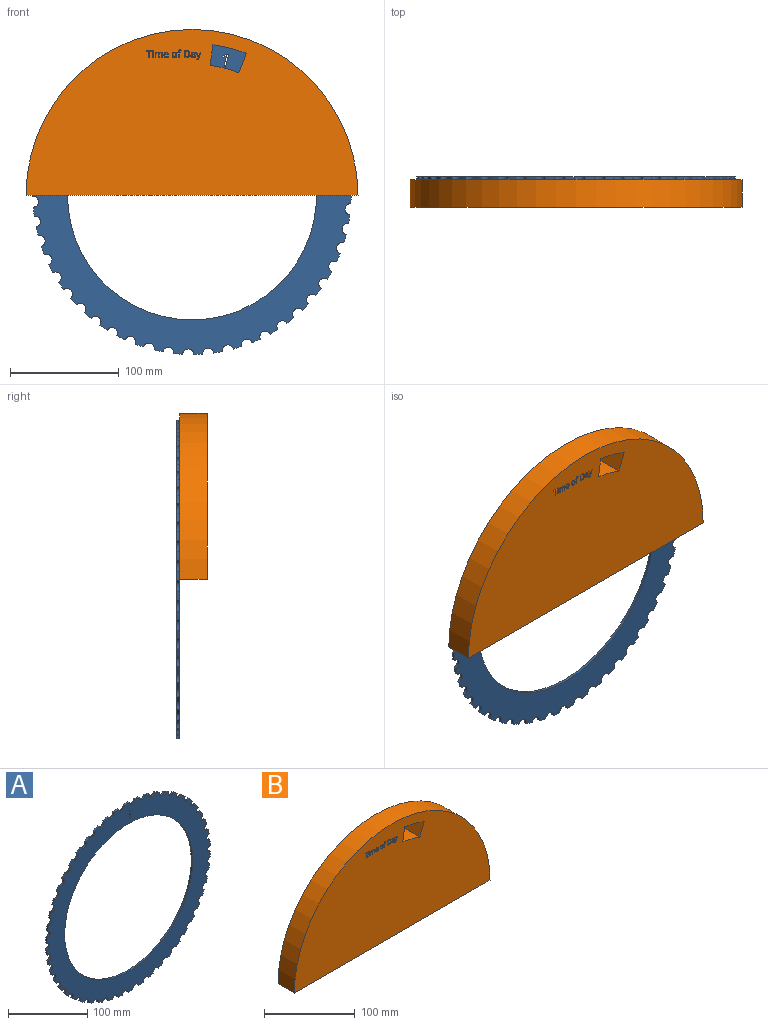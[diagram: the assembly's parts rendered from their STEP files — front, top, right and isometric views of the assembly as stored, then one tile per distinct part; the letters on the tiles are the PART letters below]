
ASSEMBLY  parts=2 mates=1
PART A: 112 faces, bbox 292.1x2.5x292.1 mm
  f0: plane 292.1x292.08mm, normal (0,-1,0), area 23935.8mm2, adj f2,f3,f4,f5,f6,f7,f8,f9
  f1: plane 292.1x292.08mm, normal (0,1,0), area 23935.8mm2, adj f2,f3,f4,f5,f6,f7,f8,f9
  f2: cylinder r=146.05mm len=7.98mm, axis (0,1,0), area 20.8mm2, adj f0,f1,f5,f101
  f3: cylinder r=146.05mm len=7.68mm, axis (0,1,0), area 20.8mm2, adj f0,f1,f4,f5
  f4: cylinder r=5.08mm len=9.69mm, axis (0,-1,0), area 40.1mm2, adj f0,f1,f3,f6
  f5: cylinder r=5.08mm len=9.92mm, axis (0,-1,0), area 40.1mm2, adj f0,f1,f2,f3
  f6: cylinder r=146.05mm len=7.27mm, axis (0,1,0), area 20.8mm2, adj f0,f1,f4,f9
  f7: cylinder r=146.05mm len=6.73mm, axis (0,1,0), area 20.8mm2, adj f0,f1,f8,f9
  f8: cylinder r=5.08mm len=9.01mm, axis (0,-1,0), area 40.1mm2, adj f0,f1,f7,f10
  f9: cylinder r=5.08mm len=9.38mm, axis (0,-1,0), area 40.1mm2, adj f0,f1,f6,f7
  f10: cylinder r=146.05mm len=6.1mm, axis (0,1,0), area 20.8mm2, adj f0,f1,f8,f13
  f11: cylinder r=146.05mm len=6.19mm, axis (0,1,0), area 20.8mm2, adj f0,f1,f12,f13
  f12: cylinder r=5.08mm len=9.07mm, axis (0,-1,0), area 40.1mm2, adj f0,f1,f11,f14
  f13: cylinder r=5.08mm len=8.64mm, axis (0,-1,0), area 40.1mm2, adj f0,f1,f10,f11
  f14: cylinder r=146.05mm len=6.82mm, axis (0,1,0), area 20.8mm2, adj f0,f1,f12,f17
  f15: cylinder r=146.05mm len=7.33mm, axis (0,1,0), area 20.8mm2, adj f0,f1,f16,f17
  f16: cylinder r=5.08mm len=9.73mm, axis (0,-1,0), area 40.1mm2, adj f0,f1,f15,f18
  f17: cylinder r=5.08mm len=9.43mm, axis (0,-1,0), area 40.1mm2, adj f0,f1,f14,f15
  f18: cylinder r=146.05mm len=7.73mm, axis (0,1,0), area 20.8mm2, adj f0,f1,f16,f21
  f19: cylinder r=146.05mm len=8.01mm, axis (0,1,0), area 20.8mm2, adj f0,f1,f20,f21
  f20: cylinder r=5.08mm len=10.09mm, axis (0,-1,0), area 40.1mm2, adj f0,f1,f19,f22
  f21: cylinder r=5.08mm len=9.95mm, axis (0,-1,0), area 40.1mm2, adj f0,f1,f18,f19
  f22: cylinder r=146.05mm len=8.16mm, axis (0,1,0), area 20.8mm2, adj f0,f1,f20,f25
  f23: cylinder r=146.05mm len=8.19mm, axis (0,1,0), area 20.8mm2, adj f0,f1,f24,f25
  f24: cylinder r=5.08mm len=10.12mm, axis (0,-1,0), area 40.1mm2, adj f0,f1,f23,f26
  f25: cylinder r=5.08mm len=10.16mm, axis (0,-1,0), area 40.1mm2, adj f0,f1,f22,f23
  f26: cylinder r=146.05mm len=8.08mm, axis (0,1,0), area 20.8mm2, adj f0,f1,f24,f29
  f27: cylinder r=146.05mm len=7.85mm, axis (0,1,0), area 20.8mm2, adj f0,f1,f28,f29
  f28: cylinder r=5.08mm len=9.81mm, axis (0,-1,0), area 40.1mm2, adj f0,f1,f27,f30
  f29: cylinder r=5.08mm len=10.01mm, axis (0,-1,0), area 40.1mm2, adj f0,f1,f26,f27
  f30: cylinder r=146.05mm len=7.49mm, axis (0,1,0), area 20.8mm2, adj f0,f1,f28,f33
  f31: cylinder r=146.05mm len=7.01mm, axis (0,1,0), area 20.8mm2, adj f0,f1,f32,f33
  f32: cylinder r=5.08mm len=9.21mm, axis (0,-1,0), area 40.1mm2, adj f0,f1,f31,f34
  f33: cylinder r=5.08mm len=9.54mm, axis (0,-1,0), area 40.1mm2, adj f0,f1,f30,f31
  f34: cylinder r=146.05mm len=6.43mm, axis (0,1,0), area 20.8mm2, adj f0,f1,f32,f37
  f35: cylinder r=146.05mm len=5.84mm, axis (0,1,0), area 20.8mm2, adj f0,f1,f36,f37
  f36: cylinder r=5.08mm len=8.86mm, axis (0,-1,0), area 40.1mm2, adj f0,f1,f35,f38
  f37: cylinder r=5.08mm len=8.8mm, axis (0,-1,0), area 40.1mm2, adj f0,f1,f34,f35
  f38: cylinder r=146.05mm len=6.52mm, axis (0,1,0), area 20.8mm2, adj f0,f1,f36,f41
  f39: cylinder r=146.05mm len=7.09mm, axis (0,1,0), area 20.8mm2, adj f0,f1,f40,f41
  f40: cylinder r=5.08mm len=9.59mm, axis (0,-1,0), area 40.1mm2, adj f0,f1,f39,f42
  f41: cylinder r=5.08mm len=9.26mm, axis (0,-1,0), area 40.1mm2, adj f0,f1,f38,f39
  f42: cylinder r=146.05mm len=7.55mm, axis (0,1,0), area 20.8mm2, adj f0,f1,f40,f45
  f43: cylinder r=146.05mm len=7.89mm, axis (0,1,0), area 20.8mm2, adj f0,f1,f44,f45
  f44: cylinder r=5.08mm len=10.03mm, axis (0,-1,0), area 40.1mm2, adj f0,f1,f43,f46
  f45: cylinder r=5.08mm len=9.85mm, axis (0,-1,0), area 40.1mm2, adj f0,f1,f42,f43
  f46: cylinder r=146.05mm len=8.1mm, axis (0,1,0), area 20.8mm2, adj f0,f1,f44,f49
  f47: cylinder r=146.05mm len=8.19mm, axis (0,1,0), area 20.8mm2, adj f0,f1,f48,f49
  f48: cylinder r=5.08mm len=10.15mm, axis (0,-1,0), area 40.1mm2, adj f0,f1,f47,f50
  f49: cylinder r=5.08mm len=10.13mm, axis (0,-1,0), area 40.1mm2, adj f0,f1,f46,f47
  f50: cylinder r=146.05mm len=8.15mm, axis (0,1,0), area 20.8mm2, adj f0,f1,f48,f53
  f51: cylinder r=146.05mm len=7.98mm, axis (0,1,0), area 20.8mm2, adj f0,f1,f52,f53
  f52: cylinder r=5.08mm len=9.92mm, axis (0,-1,0), area 40.1mm2, adj f0,f1,f51,f54
  f53: cylinder r=5.08mm len=10.07mm, axis (0,-1,0), area 40.1mm2, adj f0,f1,f50,f51
  f54: cylinder r=146.05mm len=7.68mm, axis (0,1,0), area 20.8mm2, adj f0,f1,f52,f57
  f55: cylinder r=146.05mm len=7.27mm, axis (0,1,0), area 20.8mm2, adj f0,f1,f56,f57
  f56: cylinder r=5.08mm len=9.38mm, axis (0,-1,0), area 40.1mm2, adj f0,f1,f55,f58
  f57: cylinder r=5.08mm len=9.69mm, axis (0,-1,0), area 40.1mm2, adj f0,f1,f54,f55
  f58: cylinder r=146.05mm len=6.73mm, axis (0,1,0), area 20.8mm2, adj f0,f1,f56,f61
  f59: cylinder r=146.05mm len=6.1mm, axis (0,1,0), area 20.8mm2, adj f0,f1,f60,f61
  f60: cylinder r=5.08mm len=8.64mm, axis (0,-1,0), area 40.1mm2, adj f0,f1,f59,f62
  f61: cylinder r=5.08mm len=9.01mm, axis (0,-1,0), area 40.1mm2, adj f0,f1,f58,f59
  f62: cylinder r=146.05mm len=6.19mm, axis (0,1,0), area 20.8mm2, adj f0,f1,f60,f65
  f63: cylinder r=146.05mm len=6.82mm, axis (0,1,0), area 20.8mm2, adj f0,f1,f64,f65
  f64: cylinder r=5.08mm len=9.43mm, axis (0,-1,0), area 40.1mm2, adj f0,f1,f63,f66
  f65: cylinder r=5.08mm len=9.07mm, axis (0,-1,0), area 40.1mm2, adj f0,f1,f62,f63
  f66: cylinder r=146.05mm len=7.33mm, axis (0,1,0), area 20.8mm2, adj f0,f1,f64,f69
  f67: cylinder r=146.05mm len=7.73mm, axis (0,1,0), area 20.8mm2, adj f0,f1,f68,f69
  f68: cylinder r=5.08mm len=9.95mm, axis (0,-1,0), area 40.1mm2, adj f0,f1,f67,f70
  f69: cylinder r=5.08mm len=9.73mm, axis (0,-1,0), area 40.1mm2, adj f0,f1,f66,f67
  f70: cylinder r=146.05mm len=8.01mm, axis (0,1,0), area 20.8mm2, adj f0,f1,f68,f73
  f71: cylinder r=146.05mm len=8.16mm, axis (0,1,0), area 20.8mm2, adj f0,f1,f72,f73
  f72: cylinder r=5.08mm len=10.16mm, axis (0,-1,0), area 40.1mm2, adj f0,f1,f71,f74
  f73: cylinder r=5.08mm len=10.09mm, axis (0,-1,0), area 40.1mm2, adj f0,f1,f70,f71
  f74: cylinder r=146.05mm len=8.19mm, axis (0,1,0), area 20.8mm2, adj f0,f1,f72,f77
  f75: cylinder r=146.05mm len=8.08mm, axis (0,1,0), area 20.8mm2, adj f0,f1,f76,f77
  f76: cylinder r=5.08mm len=10.01mm, axis (0,-1,0), area 40.1mm2, adj f0,f1,f75,f78
  f77: cylinder r=5.08mm len=10.12mm, axis (0,-1,0), area 40.1mm2, adj f0,f1,f74,f75
  f78: cylinder r=146.05mm len=7.85mm, axis (0,1,0), area 20.8mm2, adj f0,f1,f76,f81
  f79: cylinder r=146.05mm len=7.49mm, axis (0,1,0), area 20.8mm2, adj f0,f1,f80,f81
  f80: cylinder r=5.08mm len=9.54mm, axis (0,-1,0), area 40.1mm2, adj f0,f1,f79,f82
  f81: cylinder r=5.08mm len=9.81mm, axis (0,-1,0), area 40.1mm2, adj f0,f1,f78,f79
  f82: cylinder r=146.05mm len=7.01mm, axis (0,1,0), area 20.8mm2, adj f0,f1,f80,f85
  f83: cylinder r=146.05mm len=6.43mm, axis (0,1,0), area 20.8mm2, adj f0,f1,f84,f85
  f84: cylinder r=5.08mm len=8.8mm, axis (0,-1,0), area 40.1mm2, adj f0,f1,f83,f86
  f85: cylinder r=5.08mm len=9.21mm, axis (0,-1,0), area 40.1mm2, adj f0,f1,f82,f83
  f86: cylinder r=146.05mm len=5.84mm, axis (0,1,0), area 20.8mm2, adj f0,f1,f84,f89
  f87: cylinder r=146.05mm len=6.52mm, axis (0,1,0), area 20.8mm2, adj f0,f1,f88,f89
  f88: cylinder r=5.08mm len=9.26mm, axis (0,-1,0), area 40.1mm2, adj f0,f1,f87,f90
  f89: cylinder r=5.08mm len=8.86mm, axis (0,-1,0), area 40.1mm2, adj f0,f1,f86,f87
  f90: cylinder r=146.05mm len=7.09mm, axis (0,1,0), area 20.8mm2, adj f0,f1,f88,f93
  f91: cylinder r=146.05mm len=7.55mm, axis (0,1,0), area 20.8mm2, adj f0,f1,f92,f93
  f92: cylinder r=5.08mm len=9.85mm, axis (0,-1,0), area 40.1mm2, adj f0,f1,f91,f94
  f93: cylinder r=5.08mm len=9.59mm, axis (0,-1,0), area 40.1mm2, adj f0,f1,f90,f91
  f94: cylinder r=146.05mm len=7.89mm, axis (0,1,0), area 20.8mm2, adj f0,f1,f92,f97
  f95: cylinder r=146.05mm len=8.1mm, axis (0,1,0), area 20.8mm2, adj f0,f1,f96,f97
  f96: cylinder r=5.08mm len=10.13mm, axis (0,-1,0), area 40.1mm2, adj f0,f1,f95,f98
  f97: cylinder r=5.08mm len=10.03mm, axis (0,-1,0), area 40.1mm2, adj f0,f1,f94,f95
  f98: cylinder r=146.05mm len=8.19mm, axis (0,1,0), area 20.8mm2, adj f0,f1,f96,f102
  f99: cylinder r=114.3mm len=228.6mm, axis (0,1,0), area 1824.1mm2, adj f0,f1
  f100: cylinder r=146.05mm len=8.15mm, axis (0,1,0), area 20.8mm2, adj f0,f1,f101,f102
  f101: cylinder r=5.08mm len=10.07mm, axis (0,-1,0), area 40.1mm2, adj f0,f1,f2,f100
  f102: cylinder r=5.08mm len=10.15mm, axis (0,-1,0), area 40.1mm2, adj f0,f1,f98,f100
  f103: plane 2.54x1.37mm, normal (0,0,1), area 3.5mm2, adj f0,f1,f104,f111
  f104: plane 12.41x2.54mm, normal (-1,0,0), area 31.5mm2, adj f0,f1,f103,f105
  f105: plane 2.54x1.19mm, normal (0,0,-1), area 3mm2, adj f0,f1,f104,f106
  f106: plane 3.28x2.54mm, normal (0.61,0,-0.79), area 10.5mm2, adj f0,f1,f105,f107
  f107: plane 2.54x0.97mm, normal (0.79,0,0.61), area 3.1mm2, adj f0,f1,f106,f108
  f108: extruded ~2.54x2.02mm, area 6.6mm2, adj f0,f1,f107,f109
  f109: extruded ~2.54x0.4mm, area 1.4mm2, adj f0,f1,f108,f110
  f110: extruded ~2.54x2.09mm, area 5.3mm2, adj f0,f1,f109,f111
  f111: plane 8.84x2.54mm, normal (1,0,0), area 22.5mm2, adj f0,f1,f103,f110
PART B: 180 faces, bbox 304.8x25.4x152.4 mm
  f0: plane 304.8x152.4mm, normal (0,-1,0), area 35806.5mm2, adj f1,f2,f4,f5,f6,f7,f8,f9
  f1: cylinder r=152.4mm len=304.8mm, axis (0,1,0), area 12161mm2, adj f0,f2,f3
  f2: plane 304.8x25.4mm, normal (0,0,-1), area 7741.9mm2, adj f0,f1,f3
  f3: plane 304.8x152.4mm, normal (0,1,0), area 35920.5mm2, adj f1,f2,f176,f177,f178,f179
  f4: plane 5.08x0.79mm, normal (0,0,-1), area 4mm2, adj f0,f5,f19,f20
  f5: plane 5.08x4.87mm, normal (0.93,0,0.37), area 26.7mm2, adj f0,f4,f6,f20
  f6: plane 5.08x0.69mm, normal (0.93,0,-0.37), area 3.8mm2, adj f0,f5,f7,f20
  f7: extruded ~5.08x1.08mm, area 7.5mm2, adj f0,f6,f8,f20
  f8: extruded ~5.08x0.54mm, area 2.8mm2, adj f0,f7,f9,f20
  f9: plane 5.08x0.59mm, normal (1,0,0), area 3mm2, adj f0,f8,f10,f20
  f10: extruded ~5.08x0.66mm, area 3.4mm2, adj f0,f9,f11,f20
  f11: extruded ~5.08x1.01mm, area 5.6mm2, adj f0,f10,f12,f20
  f12: extruded ~5.08x1.16mm, area 7mm2, adj f0,f11,f13,f20
  f13: plane 5.52x5.08mm, normal (-0.94,0,0.35), area 29.9mm2, adj f0,f12,f14,f20
  f14: plane 5.08x0.79mm, normal (0,0,-1), area 4mm2, adj f0,f13,f15,f20
  f15: extruded ~5.08x3.36mm, area 18.1mm2, adj f0,f14,f16,f20
  f16: extruded ~5.08x0.77mm, area 4.1mm2, adj f0,f15,f17,f20
  f17: plane 5.08x0.04mm, normal (0,0,-1), area 0.2mm2, adj f0,f16,f18,f20
  f18: extruded ~5.08x1.37mm, area 7.3mm2, adj f0,f17,f19,f20
  f19: plane 5.08x2.76mm, normal (-0.93,0,-0.36), area 15mm2, adj f0,f4,f18,f20
  f20: plane 7.02x4.54mm, normal (0,-1,0), area 9.1mm2, adj f4,f5,f6,f7,f8,f9,f10,f11
  f21: extruded ~5.08x0.93mm, area 5.3mm2, adj f22,f39,f40,f172
  f22: extruded ~5.08x0.88mm, area 5mm2, adj f21,f23,f40,f172
  f23: extruded ~5.08x1.06mm, area 5.7mm2, adj f22,f24,f40,f172
  f24: plane 5.08x2.53mm, normal (0,0,-1), area 12.9mm2, adj f23,f39,f40,f172
  f25: extruded ~5.08x1.69mm, area 9.5mm2, adj f0,f26,f38,f40
  f26: extruded ~5.08x0.84mm, area 4.3mm2, adj f0,f25,f27,f40
  f27: extruded ~5.08x0.74mm, area 3.9mm2, adj f0,f26,f28,f40
  f28: plane 5.08x0.65mm, normal (-1,0,0), area 3.3mm2, adj f0,f27,f29,f40
  f29: extruded ~5.08x1.55mm, area 8.1mm2, adj f0,f28,f30,f40
  f30: extruded ~5.08x1.15mm, area 6.5mm2, adj f0,f29,f31,f40
  f31: extruded ~5.08x1.29mm, area 7.1mm2, adj f0,f30,f32,f40
  f32: plane 5.08x3.34mm, normal (0,0,1), area 16.9mm2, adj f0,f31,f33,f40
  f33: plane 5.08x0.46mm, normal (-1,0,0), area 2.4mm2, adj f0,f32,f34,f40
  f34: extruded ~5.08x1.58mm, area 8.7mm2, adj f0,f33,f35,f40
  f35: extruded ~5.08x1.44mm, area 8.2mm2, adj f0,f34,f36,f40
  f36: extruded ~5.08x1.55mm, area 8.9mm2, adj f0,f35,f37,f40
  f37: extruded ~5.08x1.86mm, area 10.1mm2, adj f0,f36,f38,f40
  f38: extruded ~5.08x1.82mm, area 10mm2, adj f0,f25,f37,f40
  f39: extruded ~5.08x1.05mm, area 5.8mm2, adj f21,f24,f40,f172
  f40: plane 5.02x4.1mm, normal (0,-1,0), area 9.4mm2, adj f21,f22,f23,f24,f25,f26,f27,f28
  f41: extruded ~5.08x1.42mm, area 7.6mm2, adj f42,f57,f58,f173
  f42: extruded ~5.08x1.41mm, area 7.5mm2, adj f41,f43,f58,f173
  f43: extruded ~5.08x1.09mm, area 6.3mm2, adj f42,f44,f58,f173
  f44: extruded ~5.08x1.1mm, area 6.3mm2, adj f43,f45,f58,f173
  f45: extruded ~5.08x1.4mm, area 7.5mm2, adj f44,f46,f58,f173
  f46: extruded ~5.08x1.42mm, area 7.6mm2, adj f45,f47,f58,f173
  f47: extruded ~5.08x1.09mm, area 6.3mm2, adj f46,f57,f58,f173
  f48: extruded ~5.08x1.85mm, area 10.1mm2, adj f0,f49,f56,f58
  f49: extruded ~5.08x1.83mm, area 10mm2, adj f0,f48,f50,f58
  f50: extruded ~5.08x1.61mm, area 9.2mm2, adj f0,f49,f51,f58
  f51: extruded ~5.08x1.64mm, area 9.3mm2, adj f0,f50,f52,f58
  f52: extruded ~5.08x1.84mm, area 10.1mm2, adj f0,f51,f53,f58
  f53: extruded ~5.08x1.34mm, area 7mm2, adj f0,f52,f54,f58
  f54: extruded ~5.08x0.88mm, area 6mm2, adj f0,f53,f55,f58
  f55: extruded ~5.08x1.15mm, area 6.1mm2, adj f0,f54,f56,f58
  f56: extruded ~5.08x1.65mm, area 9.3mm2, adj f0,f48,f55,f58
  f57: extruded ~5.08x1.09mm, area 6.3mm2, adj f41,f47,f58,f173
  f58: plane 5.02x4.45mm, normal (0,-1,0), area 9mm2, adj f41,f42,f43,f44,f45,f46,f47,f48
  f59: extruded ~5.08x1.9mm, area 10.5mm2, adj f60,f72,f73,f174
  f60: extruded ~5.08x1.96mm, area 10.8mm2, adj f59,f61,f73,f174
  f61: extruded ~5.08x2.02mm, area 11.1mm2, adj f60,f62,f73,f174
  f62: plane 5.08x0.92mm, normal (0,0,-1), area 4.6mm2, adj f61,f63,f73,f174
  f63: plane 5.16x5.08mm, normal (-1,0,0), area 26.2mm2, adj f62,f64,f73,f174
  f64: plane 5.08x1.09mm, normal (0,0,1), area 5.5mm2, adj f63,f72,f73,f174
  f65: extruded ~5.08x2.45mm, area 13.6mm2, adj f0,f66,f71,f73
  f66: extruded ~5.08x2.33mm, area 12.9mm2, adj f0,f65,f67,f73
  f67: extruded ~5.08x2.34mm, area 13mm2, adj f0,f66,f68,f73
  f68: plane 5.08x1.98mm, normal (0,0,-1), area 10.1mm2, adj f0,f67,f69,f73
  f69: plane 6.46x5.08mm, normal (1,0,0), area 32.8mm2, adj f0,f68,f70,f73
  f70: plane 5.08x1.79mm, normal (0,0,1), area 9.1mm2, adj f0,f69,f71,f73
  f71: extruded ~5.08x2.5mm, area 13.8mm2, adj f0,f65,f70,f73
  f72: extruded ~5.08x1.89mm, area 10.4mm2, adj f59,f64,f73,f174
  f73: plane 6.46x5.16mm, normal (0,-1,0), area 13.2mm2, adj f59,f60,f61,f62,f63,f64,f65,f66
  f74: plane 5.08x1.23mm, normal (0,0,1), area 6.3mm2, adj f0,f75,f90,f91
  f75: plane 5.08x0.57mm, normal (-1,0,0), area 2.9mm2, adj f0,f74,f76,f91
  f76: plane 5.08x1.23mm, normal (0,0,-1), area 6.3mm2, adj f0,f75,f77,f91
  f77: plane 5.08x0.31mm, normal (-1,0,0), area 1.6mm2, adj f0,f76,f78,f91
  f78: extruded ~5.08x0.89mm, area 4.7mm2, adj f0,f77,f79,f91
  f79: extruded ~5.08x0.61mm, area 3.6mm2, adj f0,f78,f80,f91
  f80: extruded ~5.08x0.72mm, area 3.8mm2, adj f0,f79,f81,f91
  f81: plane 5.08x0.59mm, normal (-0.95,0,0.31), area 3.1mm2, adj f0,f80,f82,f91
  f82: extruded ~5.08x0.9mm, area 4.7mm2, adj f0,f81,f83,f91
  f83: extruded ~5.08x1.79mm, area 13.8mm2, adj f0,f82,f84,f91
  f84: plane 5.08x0.27mm, normal (1,0,0), area 1.4mm2, adj f0,f83,f85,f91
  f85: plane 5.08x0.87mm, normal (0.29,0,-0.96), area 4.6mm2, adj f0,f84,f86,f91
  f86: plane 5.08x0.33mm, normal (1,0,0), area 1.7mm2, adj f0,f85,f87,f91
  f87: plane 5.08x0.87mm, normal (0,0,1), area 4.4mm2, adj f0,f86,f88,f91
  f88: plane 5.08x4.27mm, normal (1,0,0), area 21.7mm2, adj f0,f87,f89,f91
  f89: plane 5.08x0.73mm, normal (0,0,1), area 3.7mm2, adj f0,f88,f90,f91
  f90: plane 5.08x4.27mm, normal (-1,0,0), area 21.7mm2, adj f0,f74,f89,f91
  f91: plane 6.93x3.33mm, normal (0,-1,0), area 6.9mm2, adj f74,f75,f76,f77,f78,f79,f80,f81
  f92: plane 5.08x3.15mm, normal (1,0,0), area 16mm2, adj f0,f93,f119,f120
  f93: plane 5.08x0.73mm, normal (0,0,1), area 3.7mm2, adj f0,f92,f94,f120
  f94: plane 5.08x3.16mm, normal (-1,0,0), area 16mm2, adj f0,f93,f95,f120
  f95: extruded ~5.08x1.35mm, area 7.3mm2, adj f0,f94,f96,f120
  f96: extruded ~5.08x1.23mm, area 6.8mm2, adj f0,f95,f97,f120
  f97: extruded ~5.08x0.94mm, area 4.9mm2, adj f0,f96,f98,f120
  f98: extruded ~5.08x0.63mm, area 4.5mm2, adj f0,f97,f99,f120
  f99: plane 5.08x0.04mm, normal (0,0,-1), area 0.2mm2, adj f0,f98,f100,f120
  f100: extruded ~5.08x1.49mm, area 9.2mm2, adj f0,f99,f101,f120
  f101: extruded ~5.08x0.85mm, area 4.5mm2, adj f0,f100,f102,f120
  f102: extruded ~5.08x0.59mm, area 4.1mm2, adj f0,f101,f103,f120
  f103: plane 5.08x0.04mm, normal (0,0,-1), area 0.2mm2, adj f0,f102,f104,f120
  f104: plane 5.08x0.66mm, normal (-0.98,0,-0.18), area 3.4mm2, adj f0,f103,f105,f120
  f105: plane 5.08x0.6mm, normal (0,0,-1), area 3mm2, adj f0,f104,f106,f120
  f106: plane 5.08x4.84mm, normal (1,0,0), area 24.6mm2, adj f0,f105,f107,f120
  f107: plane 5.08x0.73mm, normal (0,0,1), area 3.7mm2, adj f0,f106,f108,f120
  f108: plane 5.08x2.54mm, normal (-1,0,0), area 12.9mm2, adj f0,f107,f109,f120
  f109: extruded ~5.08x1.35mm, area 7.2mm2, adj f0,f108,f110,f120
  f110: extruded ~5.08x1.01mm, area 5.7mm2, adj f0,f109,f111,f120
  f111: extruded ~5.08x0.77mm, area 4.3mm2, adj f0,f110,f112,f120
  f112: extruded ~5.08x0.87mm, area 4.7mm2, adj f0,f111,f113,f120
  f113: plane 5.08x3.15mm, normal (1,0,0), area 16mm2, adj f0,f112,f114,f120
  f114: plane 5.08x0.73mm, normal (0,0,1), area 3.7mm2, adj f0,f113,f115,f120
  f115: plane 5.08x2.71mm, normal (-1,0,0), area 13.7mm2, adj f0,f114,f116,f120
  f116: extruded ~5.08x1.21mm, area 6.5mm2, adj f0,f115,f117,f120
  f117: extruded ~5.08x1.01mm, area 5.7mm2, adj f0,f116,f118,f120
  f118: extruded ~5.08x0.77mm, area 4.3mm2, adj f0,f117,f119,f120
  f119: extruded ~5.08x0.87mm, area 4.7mm2, adj f0,f92,f118,f120
  f120: plane 6.91x4.93mm, normal (0,-1,0), area 13.3mm2, adj f92,f93,f94,f95,f96,f97,f98,f99
  f121: extruded ~5.08x0.37mm, area 2mm2, adj f0,f122,f128,f129
  f122: extruded ~5.08x0.37mm, area 2mm2, adj f0,f121,f123,f129
  f123: extruded ~5.08x0.31mm, area 1.7mm2, adj f0,f122,f124,f129
  f124: extruded ~5.08x0.3mm, area 1.7mm2, adj f0,f123,f125,f129
  f125: extruded ~5.08x0.37mm, area 2mm2, adj f0,f124,f126,f129
  f126: extruded ~5.08x0.37mm, area 2mm2, adj f0,f125,f127,f129
  f127: extruded ~5.08x0.3mm, area 1.7mm2, adj f0,f126,f128,f129
  f128: extruded ~5.08x0.31mm, area 1.7mm2, adj f0,f121,f127,f129
  f129: plane 0.98x0.87mm, normal (0,-1,0), area 0.7mm2, adj f121,f122,f123,f124,f125,f126,f127,f128
  f130: plane 5.08x0.73mm, normal (0,0,1), area 3.7mm2, adj f0,f131,f133,f134
  f131: plane 5.08x4.84mm, normal (-1,0,0), area 24.6mm2, adj f0,f130,f132,f134
  f132: plane 5.08x0.73mm, normal (0,0,-1), area 3.7mm2, adj f0,f131,f133,f134
  f133: plane 5.08x4.84mm, normal (1,0,0), area 24.6mm2, adj f0,f130,f132,f134
  f134: plane 4.84x0.73mm, normal (0,-1,0), area 3.6mm2, adj f130,f131,f132,f133
  f135: extruded ~5.08x1.08mm, area 5.9mm2, adj f136,f161,f162,f175
  f136: extruded ~5.08x0.67mm, area 3.7mm2, adj f135,f137,f162,f175
  f137: extruded ~5.08x0.61mm, area 3.4mm2, adj f136,f138,f162,f175
  f138: extruded ~5.08x0.75mm, area 4.5mm2, adj f137,f139,f162,f175
  f139: extruded ~5.08x1.26mm, area 6.6mm2, adj f138,f140,f162,f175
  f140: plane 5.08x0.73mm, normal (-0.04,0,1), area 3.7mm2, adj f139,f141,f162,f175
  f141: plane 5.08x0.44mm, normal (1,0,0), area 2.2mm2, adj f140,f161,f162,f175
  f142: plane 5.08x0.69mm, normal (0.98,0,0.21), area 3.6mm2, adj f0,f143,f160,f162
  f143: plane 5.08x0.54mm, normal (0,0,1), area 2.8mm2, adj f0,f142,f144,f162
  f144: plane 5.08x3.31mm, normal (-1,0,0), area 16.8mm2, adj f0,f143,f145,f162
  f145: extruded ~5.08x1.23mm, area 6.8mm2, adj f0,f144,f146,f162
  f146: extruded ~5.08x1.28mm, area 7mm2, adj f0,f145,f147,f162
  f147: extruded ~5.08x0.86mm, area 4.4mm2, adj f0,f146,f148,f162
  f148: extruded ~5.08x0.78mm, area 4.3mm2, adj f0,f147,f149,f162
  f149: plane 5.08x0.56mm, normal (0.93,0,0.37), area 3.1mm2, adj f0,f148,f150,f162
  f150: extruded ~5.08x1.37mm, area 7.3mm2, adj f0,f149,f151,f162
  f151: extruded ~5.08x0.79mm, area 4.3mm2, adj f0,f150,f152,f162
  f152: extruded ~5.08x0.84mm, area 4.6mm2, adj f0,f151,f153,f162
  f153: plane 5.08x0.3mm, normal (1,0,0), area 1.5mm2, adj f0,f152,f154,f162
  f154: plane 5.08x0.82mm, normal (0.03,0,-1), area 4.2mm2, adj f0,f153,f155,f162
  f155: extruded ~5.08x2.35mm, area 16mm2, adj f0,f154,f156,f162
  f156: extruded ~5.08x1.06mm, area 5.9mm2, adj f0,f155,f157,f162
  f157: extruded ~5.08x1.13mm, area 6.2mm2, adj f0,f156,f158,f162
  f158: extruded ~5.08x0.9mm, area 4.7mm2, adj f0,f157,f159,f162
  f159: extruded ~5.08x0.72mm, area 4.9mm2, adj f0,f158,f160,f162
  f160: plane 5.08x0.04mm, normal (0,0,1), area 0.2mm2, adj f0,f142,f159,f162
  f161: extruded ~5.08x1.05mm, area 5.9mm2, adj f135,f141,f162,f175
  f162: plane 5.01x3.88mm, normal (0,-1,0), area 9.2mm2, adj f135,f136,f137,f138,f139,f140,f141,f142
  f163: plane 5.08x0.75mm, normal (0,0,1), area 3.8mm2, adj f0,f164,f170,f171
  f164: plane 5.79x5.08mm, normal (-1,0,0), area 29.4mm2, adj f0,f163,f165,f171
  f165: plane 5.08x2.05mm, normal (0,0,1), area 10.4mm2, adj f0,f164,f166,f171
  f166: plane 5.08x0.67mm, normal (-1,0,0), area 3.4mm2, adj f0,f165,f167,f171
  f167: plane 5.08x4.84mm, normal (0,0,-1), area 24.6mm2, adj f0,f166,f168,f171
  f168: plane 5.08x0.67mm, normal (1,0,0), area 3.4mm2, adj f0,f167,f169,f171
  f169: plane 5.08x2.05mm, normal (0,0,1), area 10.4mm2, adj f0,f168,f170,f171
  f170: plane 5.79x5.08mm, normal (1,0,0), area 29.4mm2, adj f0,f163,f169,f171
  f171: plane 6.46x4.84mm, normal (0,-1,0), area 7.6mm2, adj f163,f164,f165,f166,f167,f168,f169,f170
  f172: plane 2.53x1.43mm, normal (0,-1,0), area 2.9mm2, adj f21,f22,f23,f24,f39
  f173: plane 3.78x2.93mm, normal (0,-1,0), area 9.2mm2, adj f41,f42,f43,f44,f45,f46,f47,f57
  f174: plane 5.16x3.61mm, normal (0,-1,0), area 16.4mm2, adj f59,f60,f61,f62,f63,f64,f72
  f175: plane 2.38x1.86mm, normal (0,-1,0), area 3.6mm2, adj f135,f136,f137,f138,f139,f140,f141,f161
  f176: cylinder r=139.7mm len=30.62mm, axis (0,-1,0), area 804.8mm2, adj f0,f3,f177,f179
  f177: plane 25.4x18.87mm, normal (0.99,0,-0.14), area 483.9mm2, adj f0,f3,f176,f178
  f178: cylinder r=120.65mm len=26.45mm, axis (0,-1,0), area 695.1mm2, adj f0,f3,f177,f179
  f179: plane 25.4x17.79mm, normal (-0.93,0,0.36), area 483.9mm2, adj f0,f3,f176,f178
PLACE A rot(axis=(0,1,0),13.4deg) t=(-82.12,13.13,-8.25)mm
PLACE B t=(-82.12,10.59,-8.25)mm fixed
MATE cylindrical A.f99 <-> B.f1  axis (0,1,0) through (-82.12,13.13,-8.25)mm
